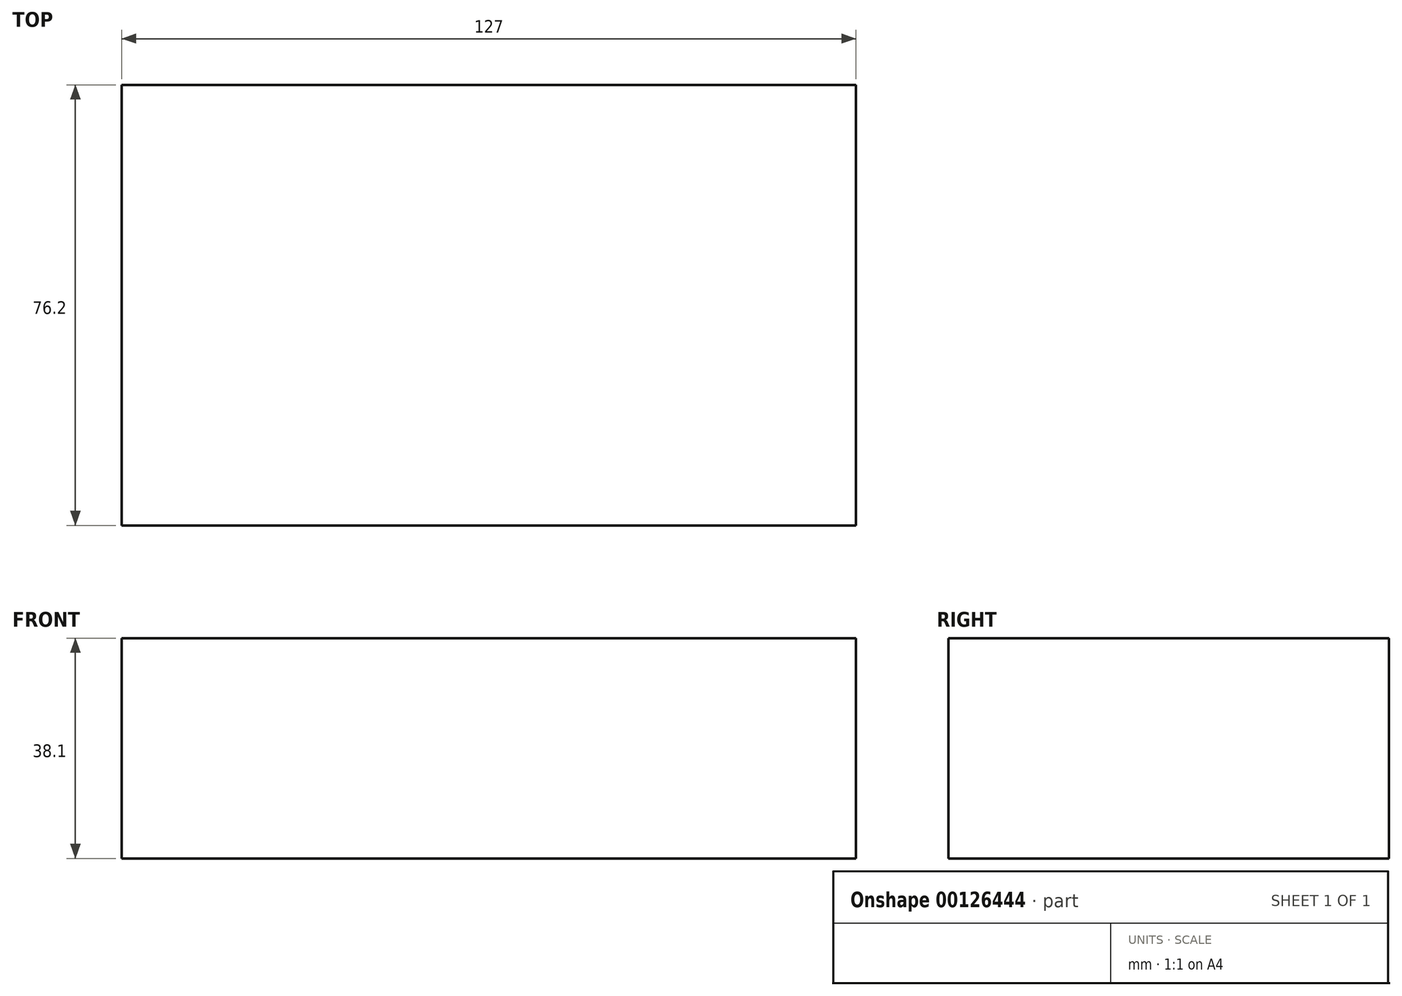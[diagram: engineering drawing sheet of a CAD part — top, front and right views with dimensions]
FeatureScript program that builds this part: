
annotation { "Feature Type Name" : "Feature", "Feature Type Description" : "" }
export const myFeature = defineFeature(function(context is Context, id is Id, definition is map)
    precondition{}
    {
        {
            var Q0;
            Q0=qCreatedBy(makeId("Top.planeOp"),FACE);
            var sketch = newSketch(context, id + "F0", { "sketchPlane" : qUnion([Q0])});
            skLineSegment(sketch, "E0.bottom", {"start": v(0, 0) * mm, "end": v(127, 0) * mm});
            skLineSegment(sketch, "E0.top", {"start": v(0, -76.2) * mm, "end": v(127, -76.2) * mm});
            skLineSegment(sketch, "E0.left", {"start": v(0, 0) * mm, "end": v(0, -76.2) * mm});
            skLineSegment(sketch, "E0.right", {"start": v(127, 0) * mm, "end": v(127, -76.2) * mm});
            skSolve(sketch);
        }
        {
            var Q0;
            Q0=makeQuery(id+"F0.imprint","IMPRINT",FACE,{"disambiguationData":[TD([[makeQuery(id+"F0.imprint","IMPRINT",EDGE,{"derivedFrom":sQuery(id+"F0.wireOp",EDGE,"E0.bottom")}),-1.0]])]});
            extrude(context, id + "F1", {"entities" : qUnion([Q0]), "depth" : 38.1 * mm});
        }
    });
